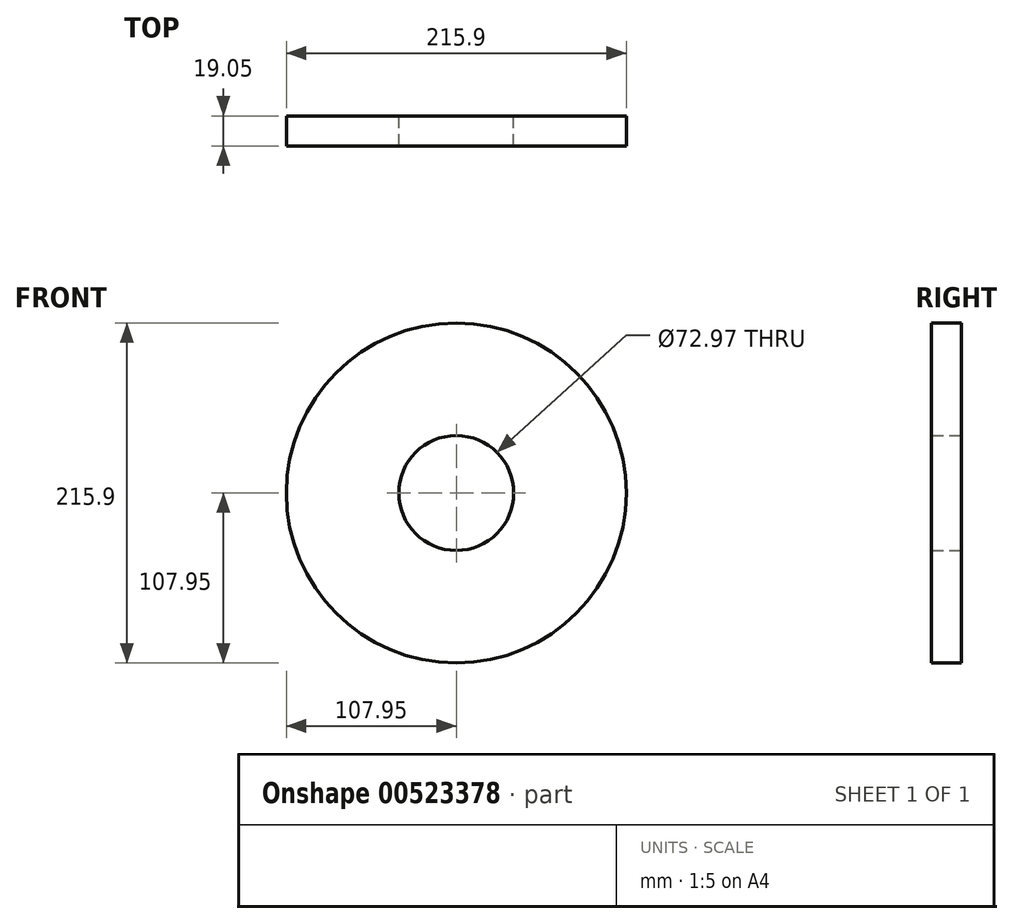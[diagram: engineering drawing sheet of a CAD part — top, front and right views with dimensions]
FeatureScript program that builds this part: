
annotation { "Feature Type Name" : "Feature", "Feature Type Description" : "" }
export const myFeature = defineFeature(function(context is Context, id is Id, definition is map)
    precondition{}
    {
        {
            var Q0;
            Q0=qCreatedBy(makeId("Front.planeOp"),FACE);
            var sketch = newSketch(context, id + "F0", { "sketchPlane" : qUnion([Q0])});
            skCircle(sketch, "E0", {"center": v(0, 0) * mm, "radius": 107.95 * mm});
            skCircle(sketch, "E1", {"center": v(0, 0) * mm, "radius": 36.49 * mm});
            skSolve(sketch);
        }
        {
            var Q0;
            Q0=makeQuery(id+"F0.imprint","IMPRINT",FACE,{"disambiguationData":[TD([[makeQuery(id+"F0.imprint","IMPRINT",EDGE,{"derivedFrom":sQuery(id+"F0.wireOp",EDGE,"E0")}),1.0]])]});
            extrude(context, id + "F1", {"entities" : qUnion([Q0]), "depth" : 19.05 * mm, "offsetDistance" : 25.4 * mm});
        }
    });
